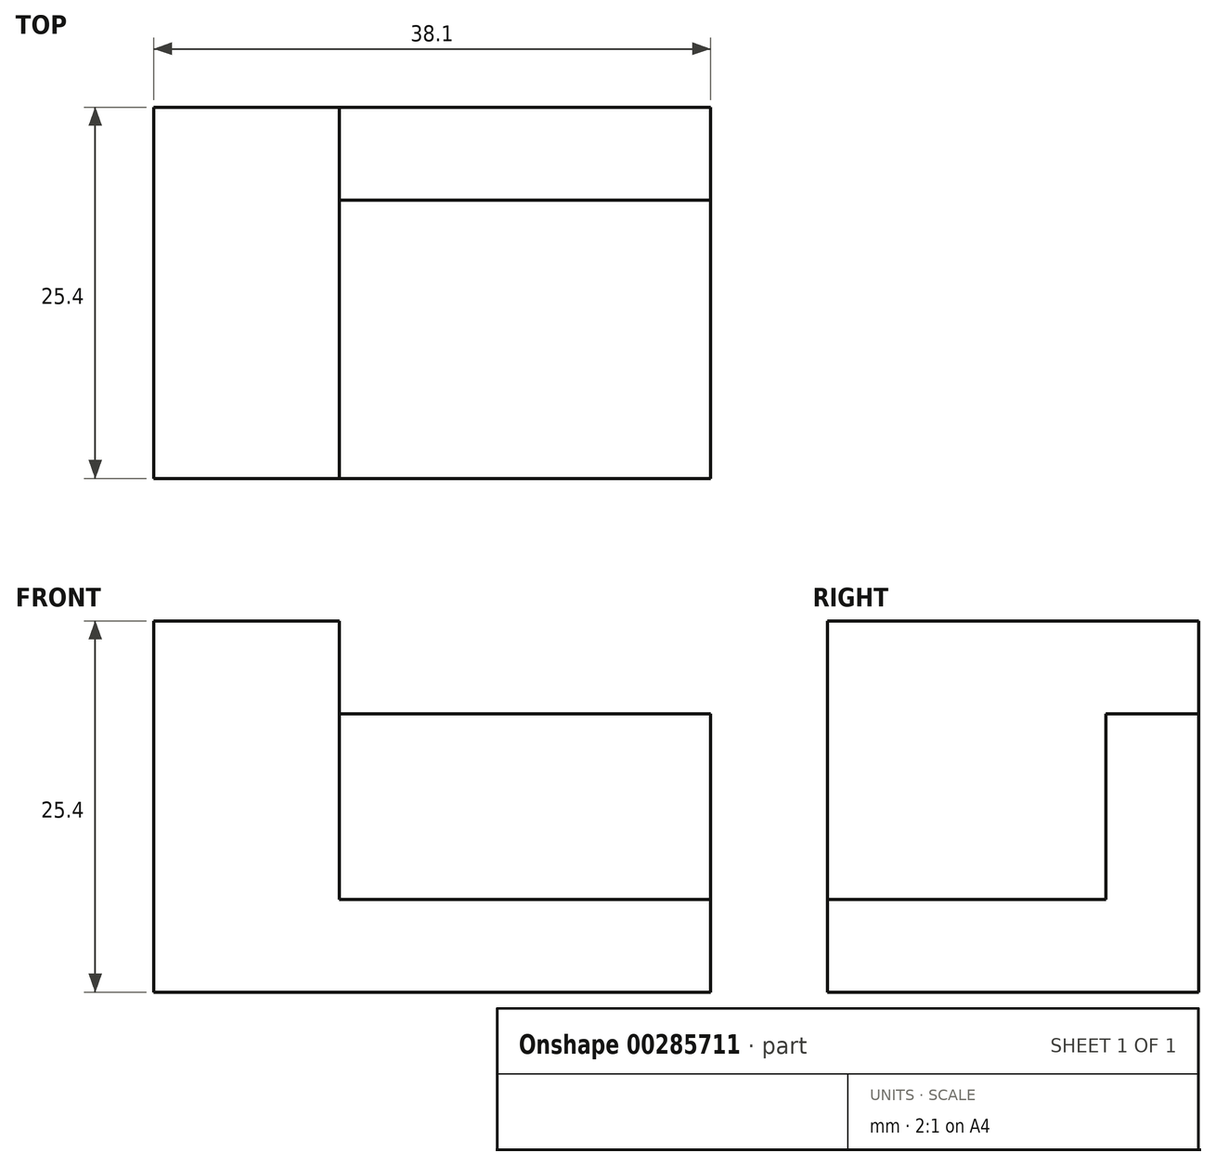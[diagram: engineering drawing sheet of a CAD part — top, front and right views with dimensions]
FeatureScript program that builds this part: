
annotation { "Feature Type Name" : "Feature", "Feature Type Description" : "" }
export const myFeature = defineFeature(function(context is Context, id is Id, definition is map)
    precondition{}
    {
        {
            var Q0;
            Q0=qCreatedBy(makeId("Right.planeOp"),FACE);
            var sketch = newSketch(context, id + "F0", { "sketchPlane" : qUnion([Q0])});
            skLineSegment(sketch, "E0.bottom", {"start": v(0, 0) * mm, "end": v(25.4, 0) * mm});
            skLineSegment(sketch, "E0.top", {"start": v(0, 25.4) * mm, "end": v(25.4, 25.4) * mm});
            skLineSegment(sketch, "E0.left", {"start": v(0, 0) * mm, "end": v(0, 25.4) * mm});
            skLineSegment(sketch, "E0.right", {"start": v(25.4, 0) * mm, "end": v(25.4, 25.4) * mm});
            skSolve(sketch);
        }
        {
            var Q0;
            Q0 = qSketchRegion(id + "F0", true);
            extrude(context, id + "F1", {"entities" : qUnion([Q0]), "depth" : 12.7 * mm});
        }
        {
            var Q0;
            Q0=makeQuery(id+"F1.opExtrude","CAP_FACE",FACE,{"disambiguationData":[OSD([sQuery(id+"F0.wireOp",EDGE,"E0.bottom"),sQuery(id+"F0.wireOp",EDGE,"E0.top"),sQuery(id+"F0.wireOp",EDGE,"E0.left"),sQuery(id+"F0.wireOp",EDGE,"E0.right")])],"isStart":false});
            var sketch = newSketch(context, id + "F2", { "sketchPlane" : qUnion([Q0])});
            skLineSegment(sketch, "E1.bottom", {"start": v(0, 0) * mm, "end": v(19.05, 0) * mm});
            skLineSegment(sketch, "E1.top", {"start": v(0, 6.35) * mm, "end": v(19.05, 6.35) * mm});
            skLineSegment(sketch, "E1.left", {"start": v(0, 0) * mm, "end": v(0, 6.35) * mm});
            skLineSegment(sketch, "E1.right", {"start": v(19.05, 0) * mm, "end": v(19.05, 6.35) * mm});
            skLineSegment(sketch, "E2.bottom", {"start": v(19.05, 0) * mm, "end": v(25.4, 0) * mm});
            skLineSegment(sketch, "E2.top", {"start": v(19.05, 19.05) * mm, "end": v(25.4, 19.05) * mm});
            skLineSegment(sketch, "E2.left", {"start": v(19.05, 0) * mm, "end": v(19.05, 19.05) * mm});
            skLineSegment(sketch, "E2.right", {"start": v(25.4, 0) * mm, "end": v(25.4, 19.05) * mm});
            skSolve(sketch);
        }
        {
            var Q0;
            {var subQ0=sQuery(id+"F2.wireOp",EDGE,"E1.bottom");Q0=makeQuery(id+"F2.imprint","IMPRINT",FACE,{"disambiguationData":[TD([[makeQuery(id+"F2.imprint","IMPRINT",EDGE,{"derivedFrom":subQ0}),1.0]])]});}
            var Q1;
            {var subQ3=sQuery(id+"F2.wireOp",EDGE,"E2.bottom");Q1=makeQuery(id+"F2.imprint","IMPRINT",FACE,{"disambiguationData":[TD([[makeQuery(id+"F2.imprint","IMPRINT",EDGE,{"derivedFrom":subQ3}),1.0]])]});}
            extrude(context, id + "F3", {"entities" : qUnion([Q0, Q1]), "operationType" : NewBodyOperationType.ADD, "depth" : 25.4 * mm});
        }
    });
